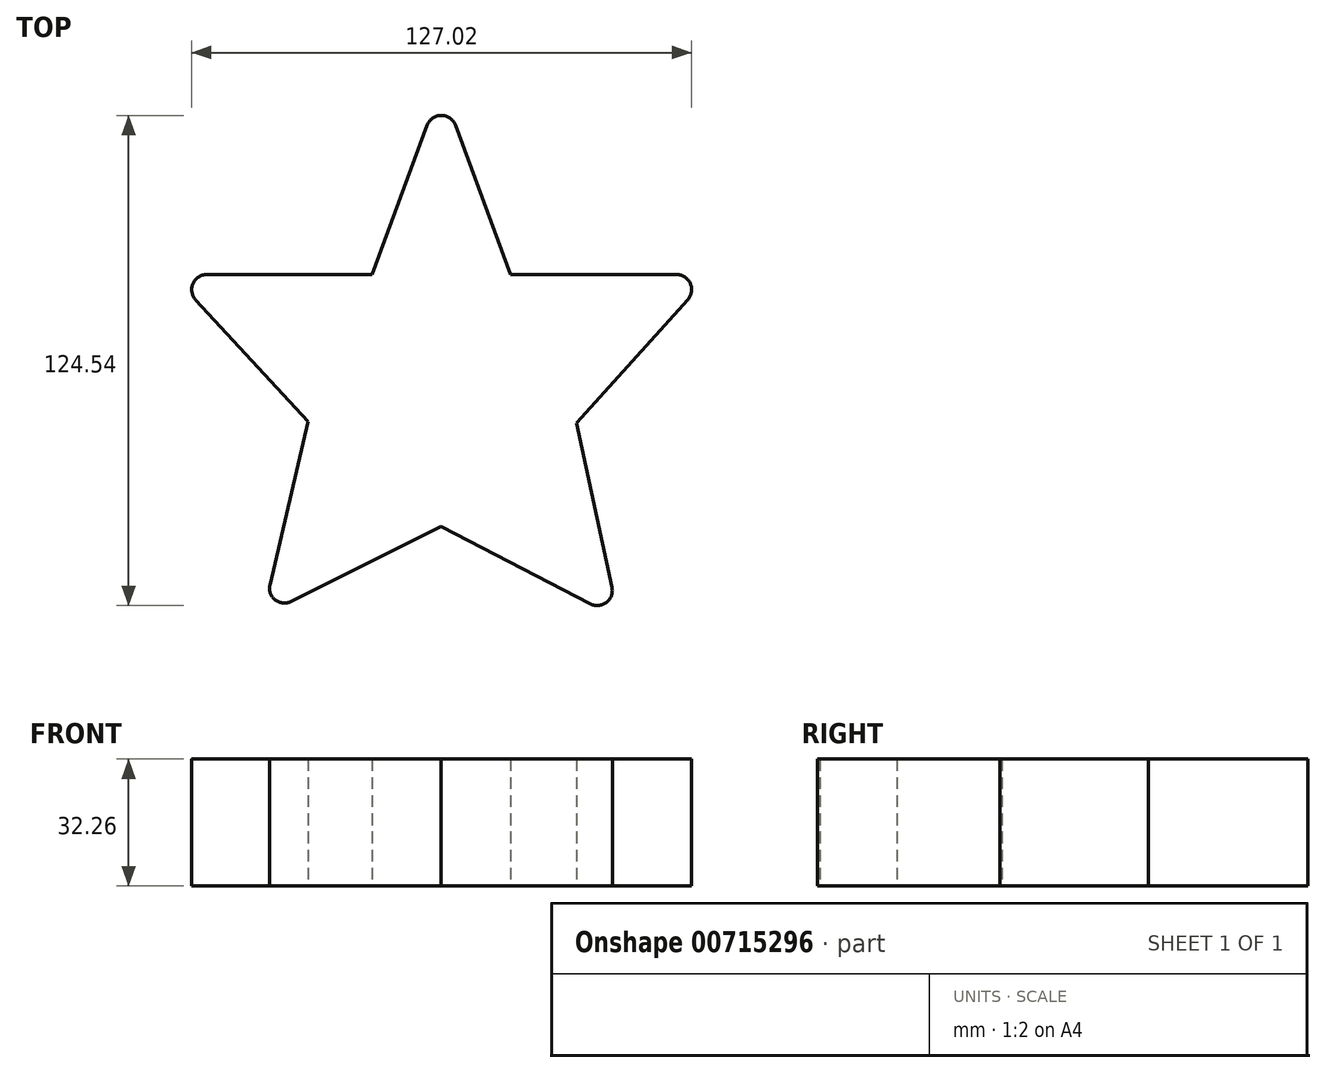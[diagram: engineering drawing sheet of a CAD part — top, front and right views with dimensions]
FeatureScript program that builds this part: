
annotation { "Feature Type Name" : "Feature", "Feature Type Description" : "" }
export const myFeature = defineFeature(function(context is Context, id is Id, definition is map)
    precondition{}
    {
        {
            var Q0;
            Q0=qCreatedBy(makeId("Top.planeOp"),FACE);
            var sketch = newSketch(context, id + "F0", { "sketchPlane" : qUnion([Q0])});
            skLineSegment(sketch, "E0", {"start": v(-17.54, 0) * mm, "end": v(-68.34, 0) * mm});
            skLineSegment(sketch, "E1", {"start": v(-68.34, 0) * mm, "end": v(-33.8, -37.25) * mm});
            skLineSegment(sketch, "E2", {"start": v(17.54, 0) * mm, "end": v(68.34, 0) * mm});
            skLineSegment(sketch, "E3", {"start": v(68.34, 0) * mm, "end": v(34.34, -37.74) * mm});
            skLineSegment(sketch, "E4", {"start": v(34.34, -37.74) * mm, "end": v(45.06, -87.4) * mm});
            skLineSegment(sketch, "E5", {"start": v(45.06, -87.4) * mm, "end": v(0, -63.94) * mm});
            skLineSegment(sketch, "E6", {"start": v(0, -63.94) * mm, "end": v(-45.4, -86.71) * mm});
            skLineSegment(sketch, "E7", {"start": v(-45.4, -86.71) * mm, "end": v(-33.8, -37.25) * mm});
            skLineSegment(sketch, "E8", {"start": v(-17.54, 0) * mm, "end": v(0, 47.67) * mm});
            skLineSegment(sketch, "E9", {"start": v(0, 47.67) * mm, "end": v(17.54, 0) * mm});
            skSolve(sketch);
        }
        {
            var Q0;
            Q0=makeQuery(id+"F0.imprint","IMPRINT",FACE,{"disambiguationData":[TD([[makeQuery(id+"F0.imprint","IMPRINT",EDGE,{"derivedFrom":sQuery(id+"F0.wireOp",EDGE,"E0")}),1.0]])]});
            extrude(context, id + "F1", {"entities" : qUnion([Q0]), "depth" : 32.26 * mm, "offsetDistance" : 25.4 * mm});
        }
        {
            var Q0;
            Q0=makeQuery(id+"F1.opExtrude","SWEPT_EDGE",EDGE,{"disambiguationData":[OSD([sQuery(id+"F0.wireOp",EDGE,"E4"),sQuery(id+"F0.wireOp",EDGE,"E5")])]});
            var Q1;
            Q1=makeQuery(id+"F1.opExtrude","SWEPT_EDGE",EDGE,{"disambiguationData":[OSD([sQuery(id+"F0.wireOp",EDGE,"E2"),sQuery(id+"F0.wireOp",EDGE,"E3")])]});
            var Q2;
            Q2=makeQuery(id+"F1.opExtrude","SWEPT_EDGE",EDGE,{"disambiguationData":[OSD([sQuery(id+"F0.wireOp",EDGE,"E8"),sQuery(id+"F0.wireOp",EDGE,"E9")])]});
            var Q3;
            Q3=makeQuery(id+"F1.opExtrude","SWEPT_EDGE",EDGE,{"disambiguationData":[OSD([sQuery(id+"F0.wireOp",EDGE,"E6"),sQuery(id+"F0.wireOp",EDGE,"E7")])]});
            var Q4;
            Q4=makeQuery(id+"F1.opExtrude","SWEPT_EDGE",EDGE,{"disambiguationData":[OSD([sQuery(id+"F0.wireOp",EDGE,"E0"),sQuery(id+"F0.wireOp",EDGE,"E1")])]});
            fillet(context, id + "F2", {"entities" : qUnion([Q0, Q1, Q2, Q3, Q4]), "radius" : 3.8 * mm, "tangentPropagation" : true, "allowEdgeOverflow" : false});
        }
    });
